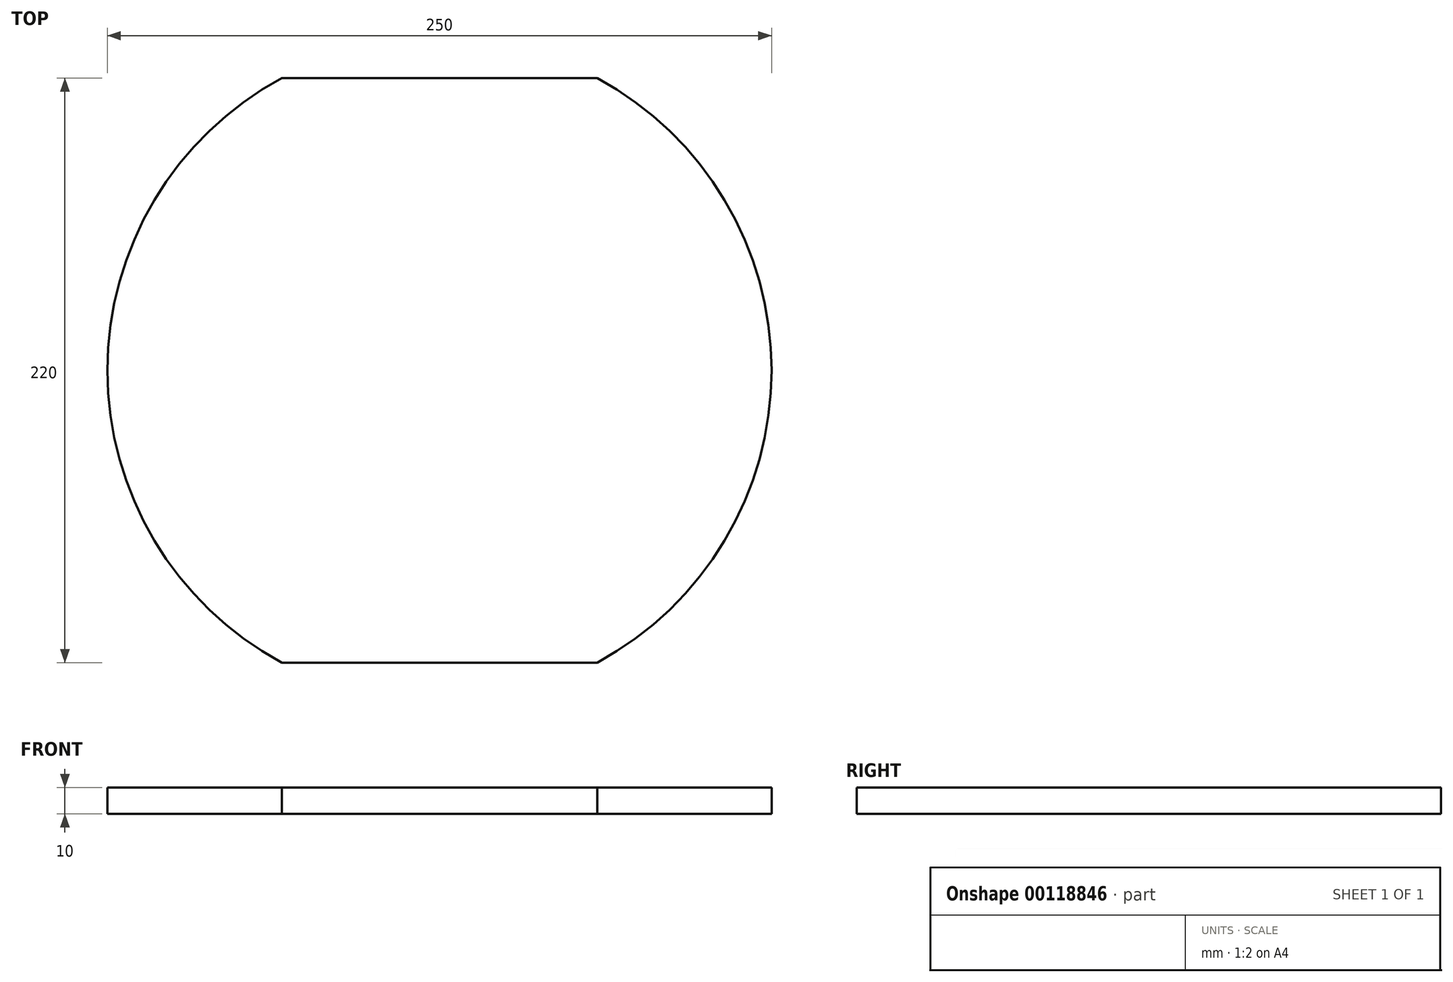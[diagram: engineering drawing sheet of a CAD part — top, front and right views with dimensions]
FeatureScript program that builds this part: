
annotation { "Feature Type Name" : "Feature", "Feature Type Description" : "" }
export const myFeature = defineFeature(function(context is Context, id is Id, definition is map)
    precondition{}
    {
        {
            var Q0;
            Q0=qCreatedBy(makeId("Top.planeOp"),FACE);
            var sketch = newSketch(context, id + "F0", { "sketchPlane" : qUnion([Q0])});
            skArc(sketch, "E0", {"start": v(-126.07, 110) * mm, "mid": v(-191.7, 0) * mm, "end": v(-126.07, -110) * mm});
            skArc(sketch, "E1", {"start": v(-7.33, -110) * mm, "mid": v(58.3, 0) * mm, "end": v(-7.33, 110) * mm});
            skLineSegment(sketch, "E2", {"start": v(-126.07, 110) * mm, "end": v(-7.33, 110) * mm});
            skLineSegment(sketch, "E3", {"start": v(-126.07, -110) * mm, "end": v(-7.33, -110) * mm});
            skSolve(sketch);
        }
        {
            var Q0;
            Q0=makeQuery(id+"F0.imprint","IMPRINT",FACE,{"disambiguationData":[TD([[makeQuery(id+"F0.imprint","IMPRINT",EDGE,{"derivedFrom":sQuery(id+"F0.wireOp",EDGE,"E0")}),1.0]])]});
            extrude(context, id + "F1", {"entities" : qUnion([Q0]), "depth" : 10 * mm});
        }
    });
